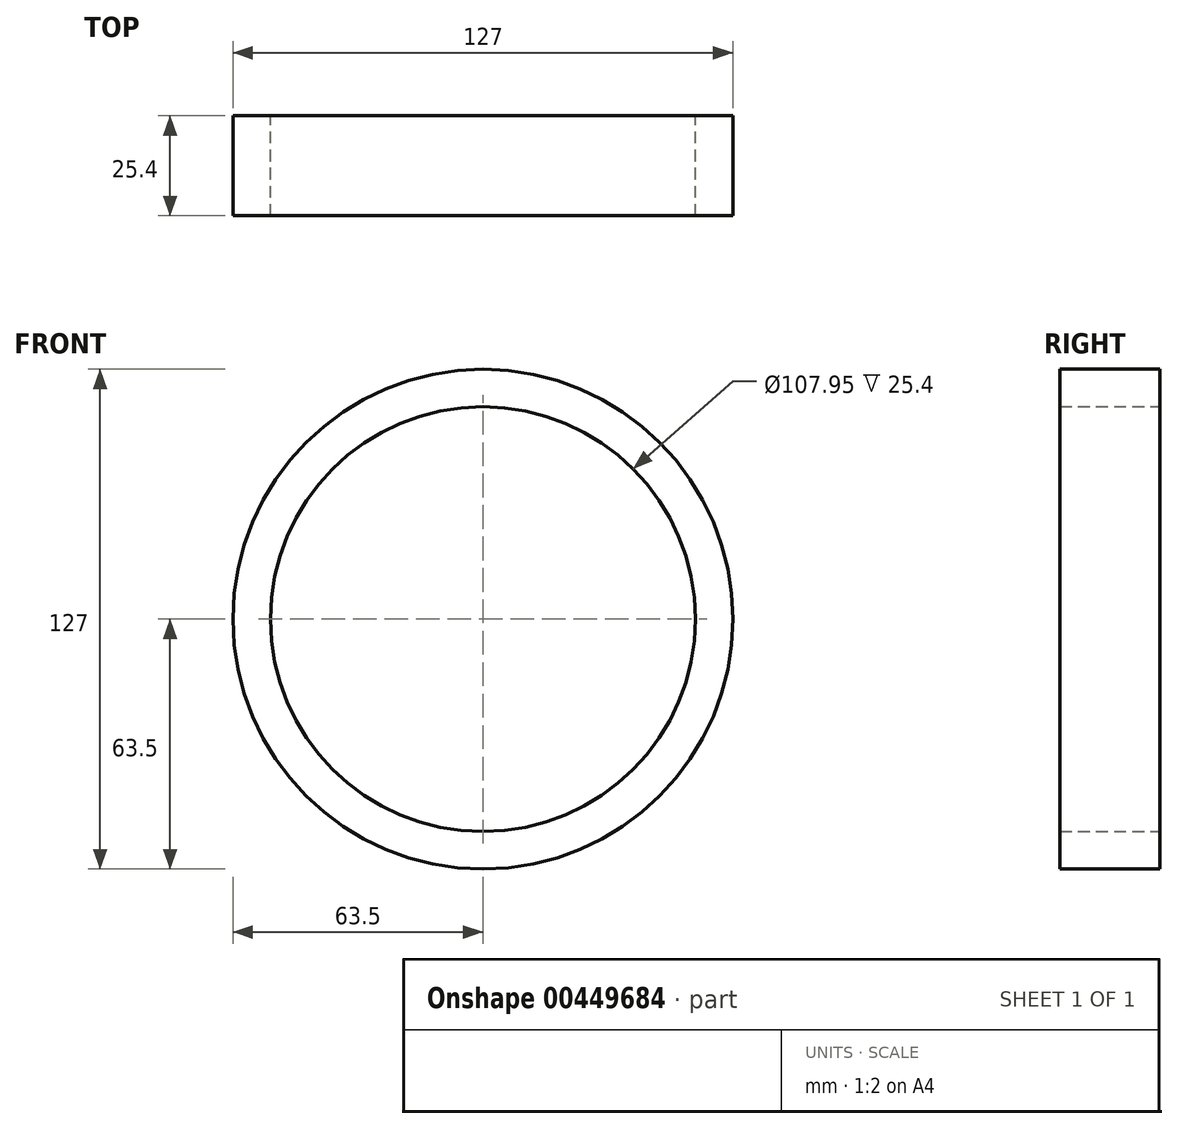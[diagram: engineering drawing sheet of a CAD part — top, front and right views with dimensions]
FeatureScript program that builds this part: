
annotation { "Feature Type Name" : "Feature", "Feature Type Description" : "" }
export const myFeature = defineFeature(function(context is Context, id is Id, definition is map)
    precondition{}
    {
        {
            var Q0;
            Q0=qCreatedBy(makeId("Front.planeOp"),FACE);
            var sketch = newSketch(context, id + "F0", { "sketchPlane" : qUnion([Q0])});
            skCircle(sketch, "E0", {"center": v(0, 0) * mm, "radius": 63.5 * mm});
            skCircle(sketch, "E1", {"center": v(0, 0) * mm, "radius": 53.98 * mm});
            skSolve(sketch);
        }
        {
            var Q0;
            Q0=makeQuery(id+"F0.imprint","IMPRINT",FACE,{"disambiguationData":[TD([[makeQuery(id+"F0.imprint","IMPRINT",EDGE,{"derivedFrom":sQuery(id+"F0.wireOp",EDGE,"E0")}),1.0]])]});
            extrude(context, id + "F1", {"entities" : qUnion([Q0]), "depth" : 25.4 * mm});
        }
    });
